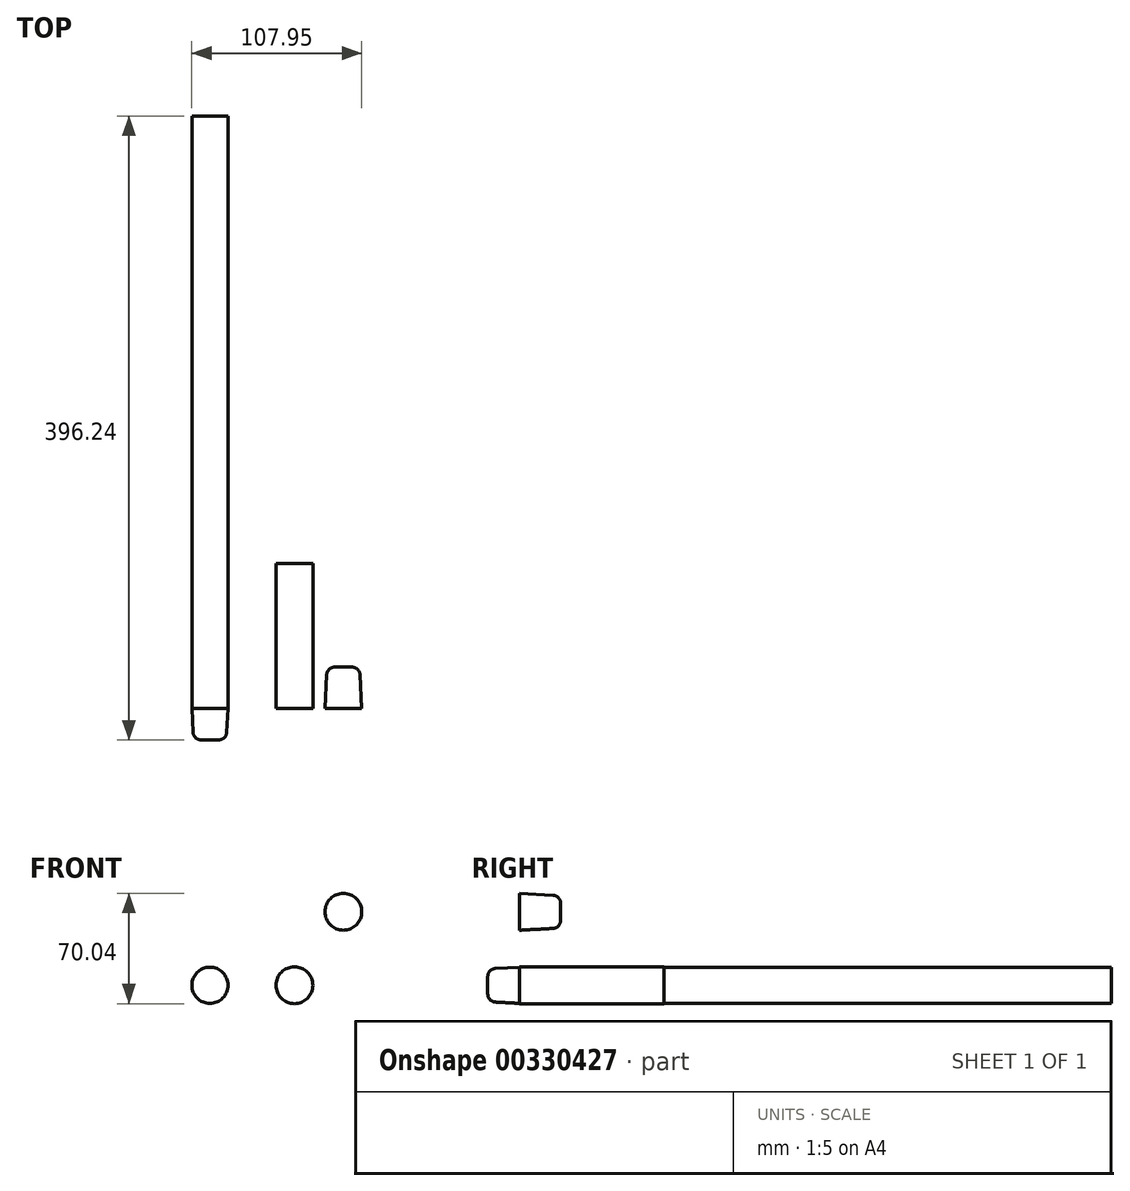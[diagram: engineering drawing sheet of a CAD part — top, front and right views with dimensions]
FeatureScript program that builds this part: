
annotation { "Feature Type Name" : "Feature", "Feature Type Description" : "" }
export const myFeature = defineFeature(function(context is Context, id is Id, definition is map)
    precondition{}
    {
        {
            var Q0;
            Q0=qCreatedBy(makeId("Front.planeOp"),FACE);
            var sketch = newSketch(context, id + "F0", { "sketchPlane" : qUnion([Q0])});
            skCircle(sketch, "E0", {"center": v(-37.9, 12.66) * mm, "radius": 11.48 * mm});
            skCircle(sketch, "E1", {"center": v(15.83, 12.66) * mm, "radius": 11.7 * mm});
            skSolve(sketch);
        }
        {
            var Q0;
            Q0=makeQuery(id+"F0.imprint","IMPRINT",FACE,{"disambiguationData":[TD([[makeQuery(id+"F0.imprint","IMPRINT",EDGE,{"derivedFrom":sQuery(id+"F0.wireOp",EDGE,"E0")}),1.0]])]});
            extrude(context, id + "F1", {"entities" : qUnion([Q0]), "oppositeDirection" : true, "depth" : 376.17 * mm});
        }
        {
            var Q0;
            Q0=makeQuery(id+"F1.opExtrude","CAP_FACE",FACE,{"disambiguationData":[OSD([sQuery(id+"F0.wireOp",EDGE,"E0")])],"isStart":true});
            var sketch = newSketch(context, id + "F2", { "sketchPlane" : qUnion([Q0])});
            skCircle(sketch, "E2", {"center": v(-37.9, 12.66) * mm, "radius": 11.7 * mm});
            skSolve(sketch);
        }
        {
            var Q0;
            Q0=makeQuery(id+"F2.imprint","IMPRINT",FACE,{"disambiguationData":[TD([[makeQuery(id+"F2.imprint","IMPRINT",EDGE,{"derivedFrom":makeQuery(id+"F1.opExtrude","CAP_EDGE",EDGE,{"disambiguationData":[OSD([sQuery(id+"F0.wireOp",EDGE,"E0")])],"isStart":true})}),1.0]])]});
            extrude(context, id + "F3", {"entities" : qUnion([Q0]), "operationType" : NewBodyOperationType.ADD, "depth" : 20.07 * mm, "hasDraft" : true, "draftAngle" : 3 * degree, "draftPullDirection" : true});
        }
        {
            var Q0;
            Q0=makeQuery(id+"F3.opExtrude","CAP_FACE",FACE,{"disambiguationData":[OSD([sQuery(id+"F0.wireOp",EDGE,"E0")])],"isStart":false});
            fillet(context, id + "F4", {"entities" : qUnion([Q0]), "radius" : 5.08 * mm, "tangentPropagation" : true, "allowEdgeOverflow" : false});
        }
        {
            var Q0;
            Q0=makeQuery(id+"F0.imprint","IMPRINT",FACE,{"disambiguationData":[TD([[makeQuery(id+"F0.imprint","IMPRINT",EDGE,{"derivedFrom":sQuery(id+"F0.wireOp",EDGE,"E1")}),1.0]])]});
            extrude(context, id + "F5", {"entities" : qUnion([Q0]), "oppositeDirection" : true, "depth" : 91.95 * mm});
        }
        {
            var Q0;
            Q0=qCreatedBy(makeId("Front.planeOp"),FACE);
            var sketch = newSketch(context, id + "F6", { "sketchPlane" : qUnion([Q0])});
            skCircle(sketch, "E3", {"center": v(46.87, 59.31) * mm, "radius": 11.7 * mm});
            skSolve(sketch);
        }
        {
            var Q0;
            Q0=makeQuery(id+"F6.imprint","IMPRINT",FACE,{"disambiguationData":[TD([[makeQuery(id+"F6.imprint","IMPRINT",EDGE,{"derivedFrom":sQuery(id+"F6.wireOp",EDGE,"E3")}),1.0]])]});
            extrude(context, id + "F7", {"entities" : qUnion([Q0]), "oppositeDirection" : true, "depth" : 26.16 * mm, "hasDraft" : true, "draftAngle" : 3 * degree, "draftPullDirection" : true});
        }
        {
            var Q0;
            Q0=makeQuery(id+"F7.opExtrude","CAP_EDGE",EDGE,{"disambiguationData":[OSD([sQuery(id+"F6.wireOp",EDGE,"E3")])],"isStart":false});
            fillet(context, id + "F8", {"entities" : qUnion([Q0]), "radius" : 5.08 * mm, "tangentPropagation" : true, "allowEdgeOverflow" : false});
        }
    });
